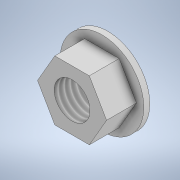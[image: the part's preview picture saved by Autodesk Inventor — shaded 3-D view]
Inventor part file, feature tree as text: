
AUTODESK INVENTOR PART (.ipt)
format: ipt  version: 2021 (Build 250183000, 183)  size: 122,880 bytes
history: native  units: in
note: dims shown in document units (in); Inventor stores cm internally (conversion verified against a paired STEP export)
features: other x2, thread x1
ambient origin geometry x8: Origin, YZ Plane, XZ Plane, XY Plane, X Axis, Y Axis, Z Axis, Center Point
bodies: Body1 (feature_tree)
feature tree (3):
  other  "Sólido2"
  thread  "Rosca1"  [1 undecoded]
  other  "Sólido1"
note: 1 required parameter value undecoded (feature->parameter linkage not recoverable at this tier; creation-order binding heuristic only, values carry confidence <= 0.55)
